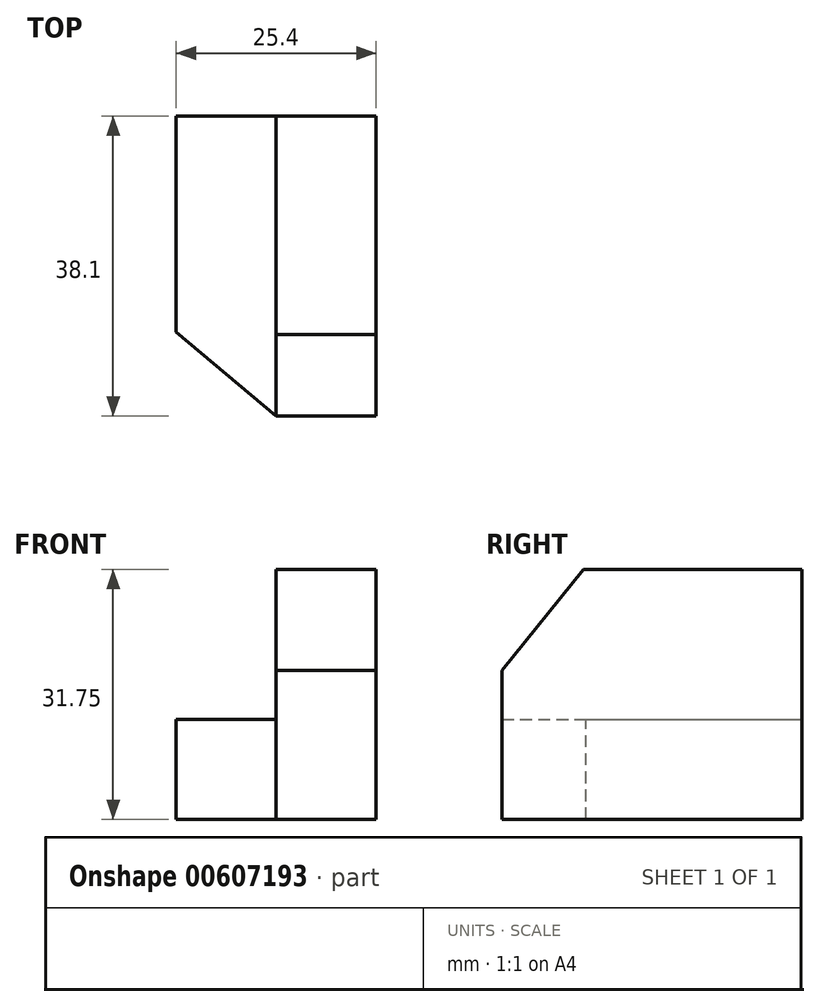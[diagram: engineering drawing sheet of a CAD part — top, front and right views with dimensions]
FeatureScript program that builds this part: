
annotation { "Feature Type Name" : "Feature", "Feature Type Description" : "" }
export const myFeature = defineFeature(function(context is Context, id is Id, definition is map)
    precondition{}
    {
        {
            var Q0;
            Q0=qCreatedBy(makeId("Front.planeOp"),FACE);
            var sketch = newSketch(context, id + "F0", { "sketchPlane" : qUnion([Q0])});
            skLineSegment(sketch, "E0", {"start": v(0, 0) * mm, "end": v(25.4, 0) * mm});
            skLineSegment(sketch, "E1", {"start": v(25.4, 0) * mm, "end": v(25.4, 31.75) * mm});
            skLineSegment(sketch, "E2", {"start": v(25.4, 31.75) * mm, "end": v(12.7, 31.75) * mm});
            skLineSegment(sketch, "E3", {"start": v(12.7, 31.75) * mm, "end": v(12.7, 12.7) * mm});
            skLineSegment(sketch, "E4", {"start": v(12.7, 12.7) * mm, "end": v(0, 12.7) * mm});
            skLineSegment(sketch, "E5", {"start": v(0, 12.7) * mm, "end": v(0, 0) * mm});
            skSolve(sketch);
        }
        {
            var Q0;
            Q0=makeQuery(id+"F0.imprint","IMPRINT",FACE,{"disambiguationData":[TD([[makeQuery(id+"F0.imprint","IMPRINT",EDGE,{"derivedFrom":sQuery(id+"F0.wireOp",EDGE,"E0")}),1.0]])]});
            extrude(context, id + "F1", {"entities" : qUnion([Q0]), "depth" : 38.1 * mm, "offsetDistance" : 25.4 * mm});
        }
        {
            var Q0;
            Q0=makeQuery(id+"F1.opExtrude","SWEPT_FACE",FACE,{"disambiguationData":[OSD([sQuery(id+"F0.wireOp",EDGE,"E4")])]});
            var sketch = newSketch(context, id + "F2", { "sketchPlane" : qUnion([Q0])});
            skLineSegment(sketch, "E6", {"start": v(12.7, -38.1) * mm, "end": v(0, -27.45) * mm});
            skSolve(sketch);
        }
        {
            var Q0;
            {var subQ0=sQuery(id+"F2.wireOp",EDGE,"E6");Q0=makeQuery(id+"F2.imprint","IMPRINT",FACE,{"disambiguationData":[TD([[makeQuery(id+"F2.imprint","IMPRINT",EDGE,{"derivedFrom":subQ0}),1.0]])]});}
            extrude(context, id + "F3", {"entities" : qUnion([Q0]), "operationType" : NewBodyOperationType.REMOVE, "oppositeDirection" : true, "depth" : 25.4 * mm, "offsetDistance" : 25.4 * mm});
        }
        {
            var Q0;
            Q0=makeQuery(id+"F1.opExtrude","SWEPT_FACE",FACE,{"disambiguationData":[OSD([sQuery(id+"F0.wireOp",EDGE,"E3")])]});
            var sketch = newSketch(context, id + "F4", { "sketchPlane" : qUnion([Q0])});
            skLineSegment(sketch, "E7", {"start": v(38.1, 18.93) * mm, "end": v(27.74, 31.75) * mm});
            skSolve(sketch);
        }
        {
            var Q0;
            {var subQ0=sQuery(id+"F4.wireOp",EDGE,"E7");Q0=makeQuery(id+"F4.imprint","IMPRINT",FACE,{"disambiguationData":[TD([[makeQuery(id+"F4.imprint","IMPRINT",EDGE,{"derivedFrom":subQ0}),-1.0]])]});}
            extrude(context, id + "F5", {"entities" : qUnion([Q0]), "operationType" : NewBodyOperationType.REMOVE, "oppositeDirection" : true, "depth" : 25.4 * mm, "offsetDistance" : 25.4 * mm});
        }
    });
